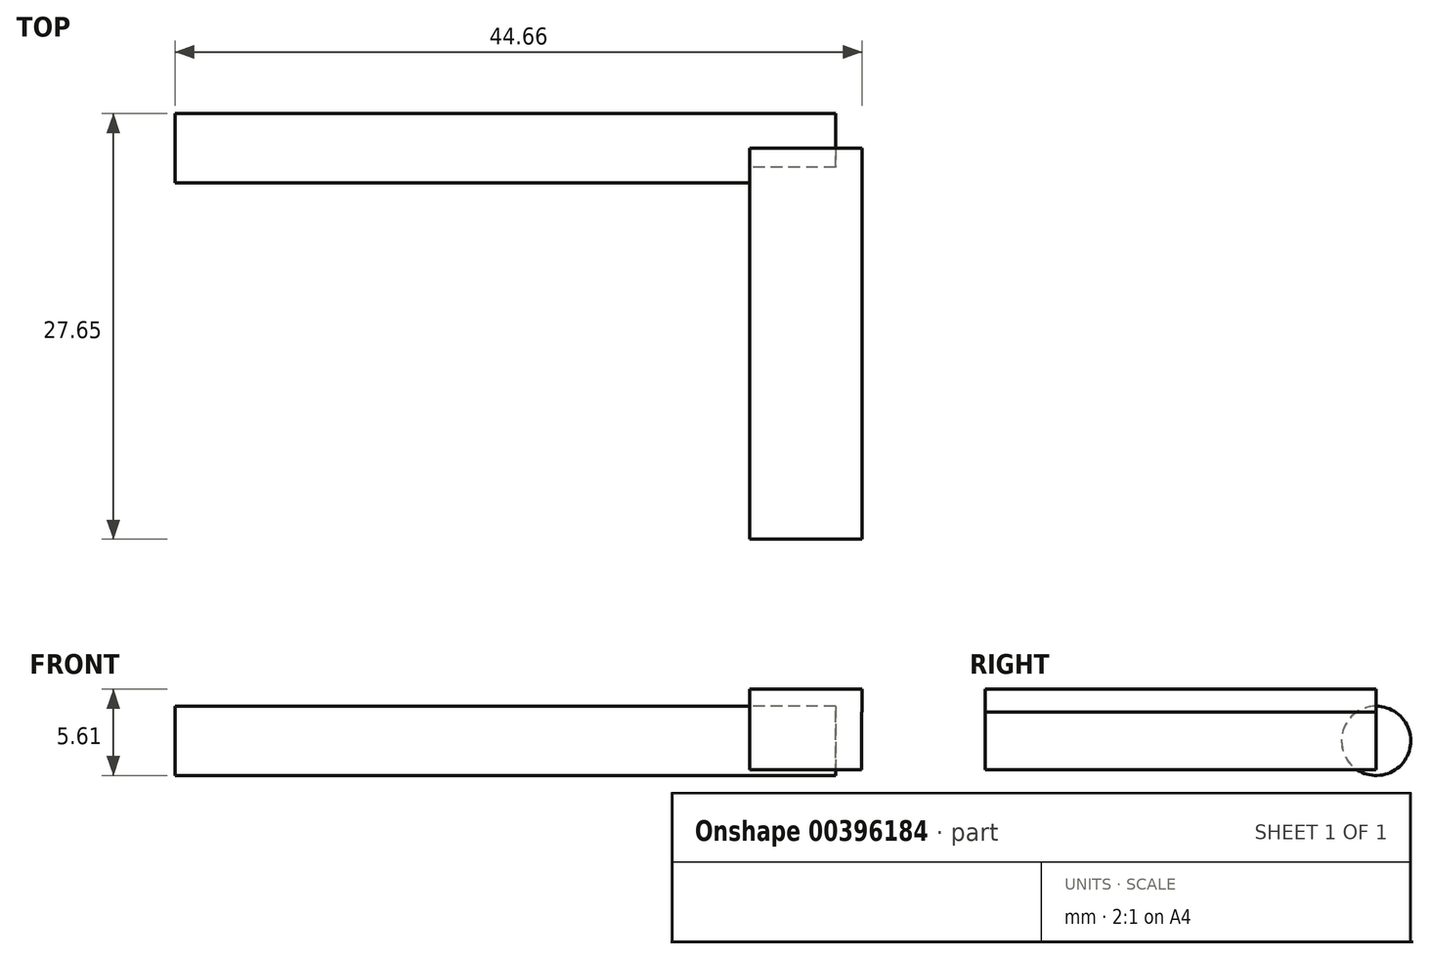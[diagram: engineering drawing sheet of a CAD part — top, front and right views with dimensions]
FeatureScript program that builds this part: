
annotation { "Feature Type Name" : "Feature", "Feature Type Description" : "" }
export const myFeature = defineFeature(function(context is Context, id is Id, definition is map)
    precondition{}
    {
        {
            var Q0;
            Q0=qCreatedBy(makeId("Front.planeOp"),FACE);
            var sketch = newSketch(context, id + "F0", { "sketchPlane" : qUnion([Q0])});
            skLineSegment(sketch, "E0", {"start": v(41.29, 0) * mm, "end": v(0, 0) * mm});
            skLineSegment(sketch, "E1.bottom", {"start": v(37.34, 0) * mm, "end": v(44.64, 0) * mm});
            skLineSegment(sketch, "E1.top", {"start": v(37.34, 1.87) * mm, "end": v(44.64, 1.87) * mm});
            skLineSegment(sketch, "E1.left", {"start": v(37.34, 0) * mm, "end": v(37.34, 1.87) * mm});
            skLineSegment(sketch, "E1.right", {"start": v(44.64, 0) * mm, "end": v(44.64, 1.87) * mm});
            skLineSegment(sketch, "E2.MirrorCS", {"start": v(37.34, -1.87) * mm, "end": v(44.64, -1.87) * mm});
            skLineSegment(sketch, "E3.MirrorCS", {"start": v(44.64, 0) * mm, "end": v(44.64, -1.87) * mm});
            skLineSegment(sketch, "E4.MirrorCS", {"start": v(37.34, 0) * mm, "end": v(37.34, -1.87) * mm});
            skLineSegment(sketch, "E5.bottom", {"start": v(37.34, 1.87) * mm, "end": v(44.66, 1.87) * mm});
            skLineSegment(sketch, "E5.top", {"start": v(37.34, 3.36) * mm, "end": v(44.66, 3.36) * mm});
            skLineSegment(sketch, "E5.left", {"start": v(37.34, 1.87) * mm, "end": v(37.34, 3.36) * mm});
            skLineSegment(sketch, "E5.right", {"start": v(44.66, 1.87) * mm, "end": v(44.66, 3.36) * mm});
            skLineSegment(sketch, "E6.MirrorCS", {"start": v(37.34, -1.87) * mm, "end": v(37.34, -3.36) * mm});
            skLineSegment(sketch, "E7.MirrorCS", {"start": v(37.34, -3.36) * mm, "end": v(44.66, -3.36) * mm});
            skLineSegment(sketch, "E8.MirrorCS", {"start": v(44.66, -1.87) * mm, "end": v(44.66, -3.36) * mm});
            skSolve(sketch);
        }
        {
            var Q0;
            Q0=qCreatedBy(makeId("Right.planeOp"),FACE);
            var sketch = newSketch(context, id + "F1", { "sketchPlane" : qUnion([Q0])});
            skCircle(sketch, "E9", {"center": v(0, 0) * mm, "radius": 2.25 * mm});
            skSolve(sketch);
        }
        {
            var Q0;
            Q0=makeQuery(id+"F1.imprint","IMPRINT",FACE,{"disambiguationData":[TD([[makeQuery(id+"F1.imprint","IMPRINT",EDGE,{"derivedFrom":sQuery(id+"F1.wireOp",EDGE,"E9")}),1.0]])]});
            extrude(context, id + "F2", {"entities" : qUnion([Q0]), "depth" : 42.93 * mm, "offsetDistance" : 25.4 * mm});
        }
        {
            var Q0;
            Q0 = qSketchRegion(id + "F0", true);
            extrude(context, id + "F3", {"entities" : qUnion([Q0]), "operationType" : NewBodyOperationType.ADD, "depth" : 25.4 * mm, "offsetDistance" : 25.4 * mm});
        }
    });
